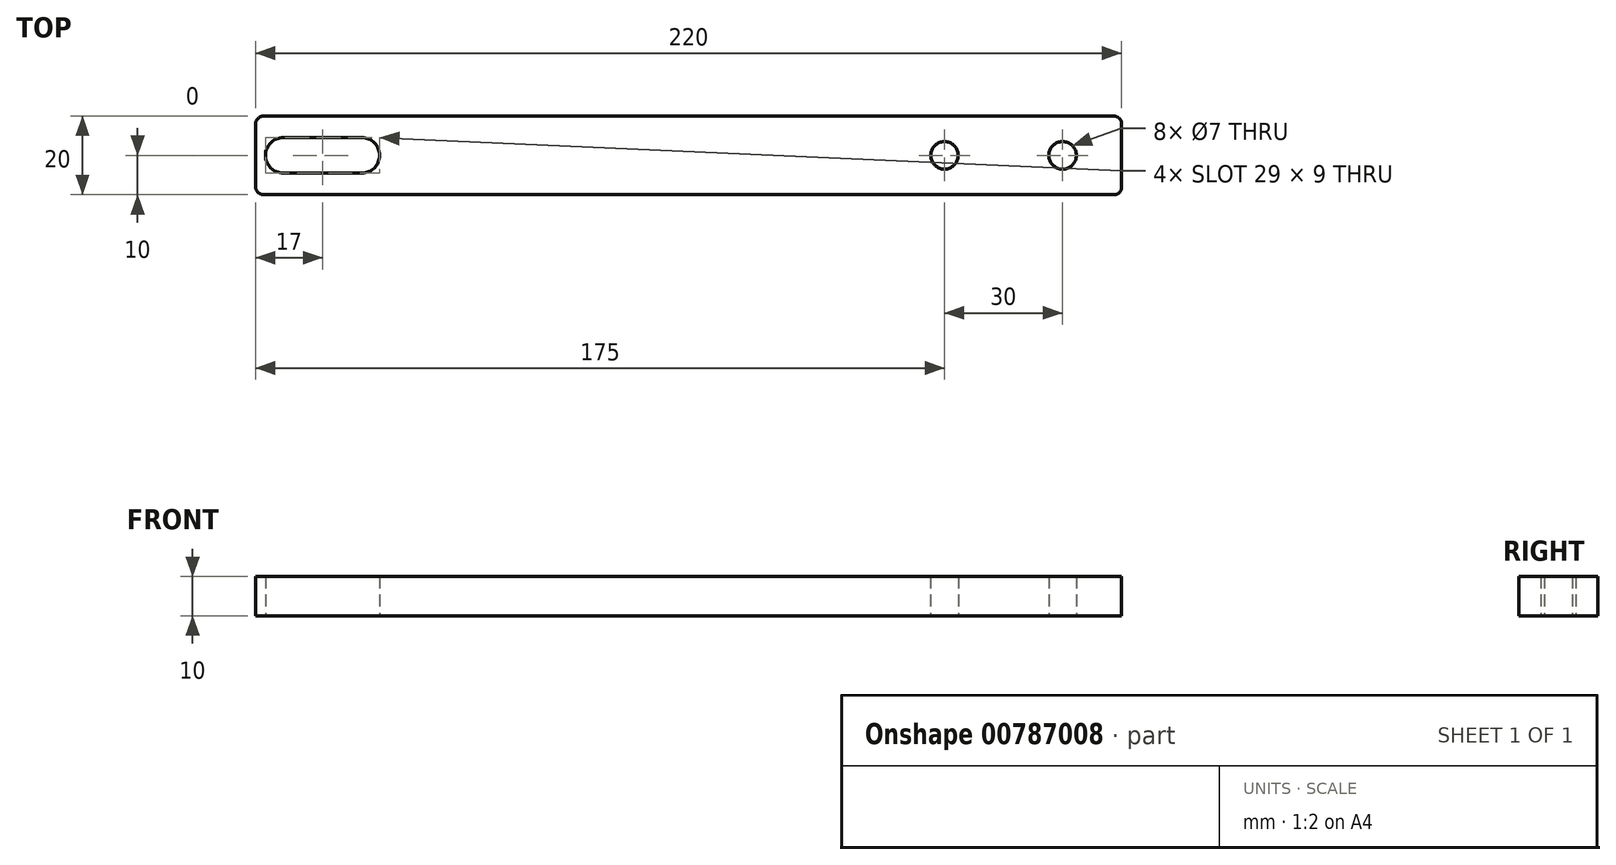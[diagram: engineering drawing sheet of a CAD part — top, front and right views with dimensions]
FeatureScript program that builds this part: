
annotation { "Feature Type Name" : "Feature", "Feature Type Description" : "" }
export const myFeature = defineFeature(function(context is Context, id is Id, definition is map)
    precondition{}
    {
        {
            var Q0;
            Q0=qCreatedBy(makeId("Top.planeOp"),FACE);
            var sketch = newSketch(context, id + "F0", { "sketchPlane" : qUnion([Q0])});
            skLineSegment(sketch, "E0.bottom", {"start": v(2, 0) * mm, "end": v(218, 0) * mm});
            skLineSegment(sketch, "E0.top", {"start": v(2, 20) * mm, "end": v(218, 20) * mm});
            skLineSegment(sketch, "E0.left", {"start": v(0, 2) * mm, "end": v(0, 18) * mm});
            skLineSegment(sketch, "E0.right", {"start": v(220, 2) * mm, "end": v(220, 18) * mm});
            skCircle(sketch, "E1", {"center": v(205, 10) * mm, "radius": 3.5 * mm});
            skCircle(sketch, "E2", {"center": v(175, 10) * mm, "radius": 3.5 * mm});
            skArc(sketch, "E3", {"start": v(7, 14.5) * mm, "mid": v(2.5, 10) * mm, "end": v(7, 5.5) * mm});
            skArc(sketch, "E4", {"start": v(27, 5.5) * mm, "mid": v(31.5, 10) * mm, "end": v(27, 14.5) * mm});
            skLineSegment(sketch, "E5", {"start": v(7, 14.5) * mm, "end": v(27, 14.5) * mm});
            skLineSegment(sketch, "E6", {"start": v(27, 5.5) * mm, "end": v(7, 5.5) * mm});
            skPoint(sketch, "E7.visualSharp", {"position": v(0, 20) * mm});
            skArc(sketch, "E7.filletArc", {"start": v(2, 20) * mm, "mid": v(0.59, 19.41) * mm, "end": v(0, 18) * mm});
            skPoint(sketch, "E8.visualSharp", {"position": v(0, 0) * mm});
            skArc(sketch, "E8.filletArc", {"start": v(0, 2) * mm, "mid": v(0.59, 0.59) * mm, "end": v(2, 0) * mm});
            skPoint(sketch, "E9.visualSharp", {"position": v(220, 0) * mm});
            skArc(sketch, "E9.filletArc", {"start": v(218, 0) * mm, "mid": v(219.41, 0.59) * mm, "end": v(220, 2) * mm});
            skPoint(sketch, "E10.visualSharp", {"position": v(220, 20) * mm});
            skArc(sketch, "E10.filletArc", {"start": v(220, 18) * mm, "mid": v(219.41, 19.41) * mm, "end": v(218, 20) * mm});
            skSolve(sketch);
        }
        {
            var Q0;
            Q0=makeQuery(id+"F0.imprint","IMPRINT",FACE,{"disambiguationData":[TD([[makeQuery(id+"F0.imprint","IMPRINT",EDGE,{"derivedFrom":sQuery(id+"F0.wireOp",EDGE,"E0.bottom")}),1.0]])]});
            extrude(context, id + "F1", {"entities" : qUnion([Q0]), "depth" : 10 * mm, "offsetDistance" : 25 * mm});
        }
    });
